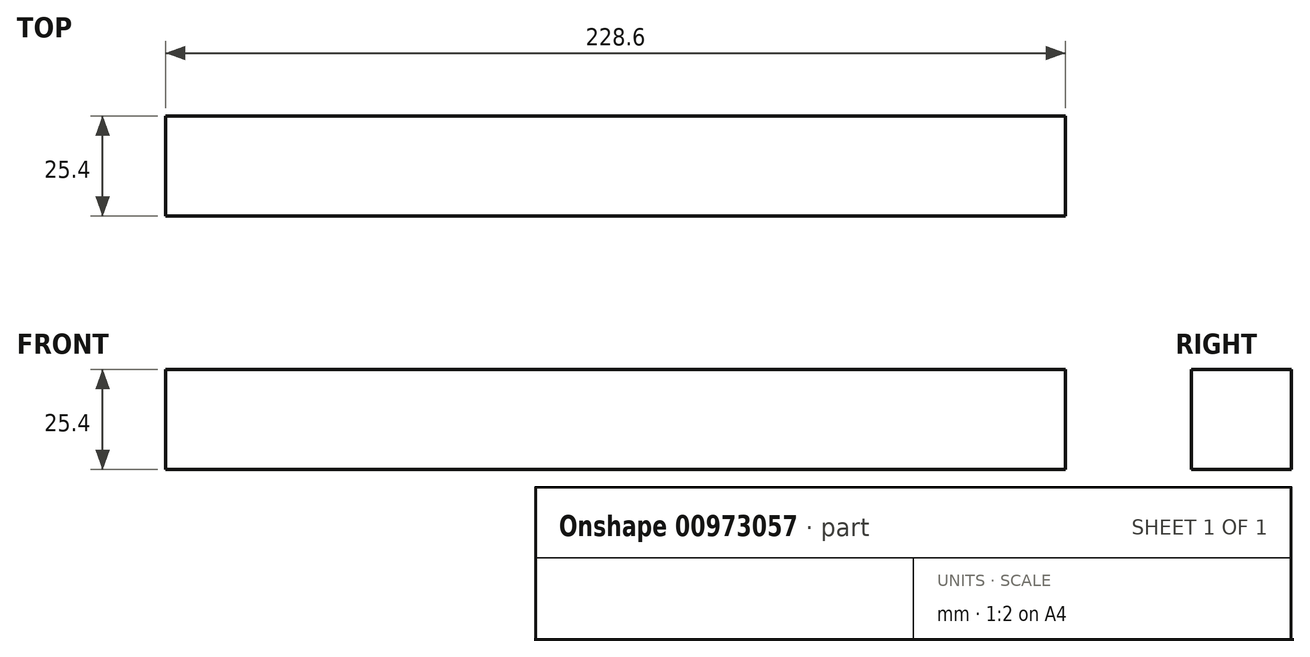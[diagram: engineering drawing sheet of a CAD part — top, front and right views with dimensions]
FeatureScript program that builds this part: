
annotation { "Feature Type Name" : "Feature", "Feature Type Description" : "" }
export const myFeature = defineFeature(function(context is Context, id is Id, definition is map)
    precondition{}
    {
        {
            var Q0;
            Q0=qCreatedBy(makeId("Right.planeOp"),FACE);
            var sketch = newSketch(context, id + "F0", { "sketchPlane" : qUnion([Q0])});
            skLineSegment(sketch, "E0.bottom", {"start": v(12.7, 12.7) * mm, "end": v(-12.7, 12.7) * mm});
            skLineSegment(sketch, "E0.top", {"start": v(12.7, -12.7) * mm, "end": v(-12.7, -12.7) * mm});
            skLineSegment(sketch, "E0.left", {"start": v(12.7, 12.7) * mm, "end": v(12.7, -12.7) * mm});
            skLineSegment(sketch, "E0.right", {"start": v(-12.7, 12.7) * mm, "end": v(-12.7, -12.7) * mm});
            skPoint(sketch, "E0.middle", {"position": v(0, 0) * mm});
            skSolve(sketch);
        }
        {
            var Q0;
            Q0=makeQuery(id+"F0.imprint","IMPRINT",FACE,{"disambiguationData":[TD([[makeQuery(id+"F0.imprint","IMPRINT",EDGE,{"derivedFrom":sQuery(id+"F0.wireOp",EDGE,"E0.bottom")}),1.0]])]});
            extrude(context, id + "F1", {"entities" : qUnion([Q0]), "depth" : 228.6 * mm, "offsetDistance" : 25.4 * mm});
        }
    });
